# Revit family: CabinetUnit1doors_40cm_Ultra-flatMirror_LEDwalllamp_Vitra_75022
name_source: partatom
category: Furniture Systems
revit_build: Autodesk Revit 2017 (Build: 20160225_1515(x64)
units: mm (PartAtom-declared; Revit-internal decimal feet)

## family parameters
Cut with Voids When Loaded = No
Host = Face
OmniClass Number = 23.40.00.00
OmniClass Title = Equipment and Furnishings
Part Type = Normal
Room Calculation Point = No
Round Connector Dimension = Use Diameter
Shared = Yes

## types (3) — shared parameters
BIMobject category = Storage
Construction Type = Wall Mounted
Default Elevation = 660 mm
Depth(mm) = 150 mm
Description = CabinetUnit1doors_40cm_Ultra-flatMirror_LEDwalllamp
Design country = Turkey
Height(mm) = 700 mm  [stored 2.29659 ft]
IFC Classification = Furnishing Element
Lighting Type = Ambiance Led Lighting
Manufacturer = Vitra
Manufacturer name = Vitra
Masterformat 2014 Code = 41 53 13
Masterformat 2014 Description = Storage Cabinets
NBS Referans Code = 35-75-08
NBS Referans Description = Bathroom Cabinets
Nominal height = 0.000
Nominal width = 0.000
OmniClass Code = 23-25 53 11 13 11
OmniClass Description = Medicine Cabinets
Product data url = https://www.vitra-bad.fr
Product family = MIA
Product group = Bathroom Furniture
Secondary Material = Mirror
Technical description = http://cdn.vitra.com.tr
Third Material = Chrome
UNSPSC Code = 30161801
UNSPSC Description = Bathroom cabinets
URL = https://vitraglobal.com
Uniclass 1.4 Code = L72141
Uniclass 1.4 Description = Cabinets
Uniclass 2.0 Code = PR-35-75-08
Uniclass 2.0 Description = Bathroom Cabinets
Uniclass 2015 Code = Pr_40_30_78_03
Uniclass 2015 Name = Bathroom cabinets
Uniformat II Code = E20
Uniformat II Description = Furnishings
Voltage = 220V
Warranty Period (Year) = 2
Width(mm) = 800 mm  [stored 2.62467 ft]
Youtube = https://www.youtube.com

## per-type parameters (varying)
| type | Article No. (default) | Color | Primary Material | Product SKU |
| CabinetUnit1doors_40cm_Ultra-flatMirror_LEDwalllamp_Vitra_75022 | 75022 | White | MattWhite | 75022 |
| CabinetUnit1doors_40cm_Ultra-flatMirror_LEDwalllamp_Vitra_75064 | 75064 | Gray Oak | Grey Oak | 75064 |
| CabinetUnit1doors_40cm_Ultra-flatMirror_LEDwalllamp_Vitra_75065 | 75065 | Gray Anthracite | Gray Anthracite | 75065 |

note: [stored X ft] marks values corroborated as IEEE doubles in the binary element streams (Revit-internal decimal feet)

## geometry (parser evidence)
native form markers: Sweep x2
no freeform markers — native parametric forms only
